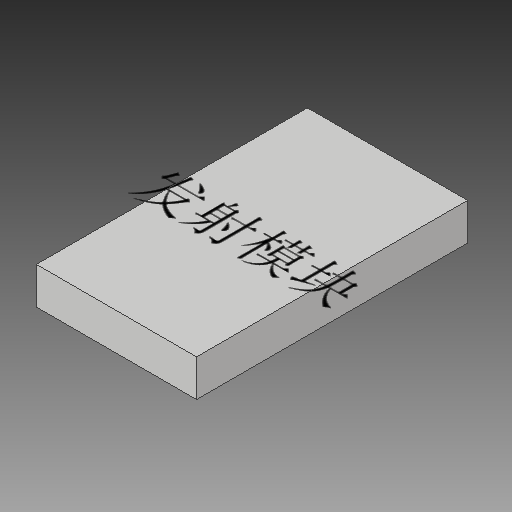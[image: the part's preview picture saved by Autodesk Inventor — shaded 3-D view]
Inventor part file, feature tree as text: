
AUTODESK INVENTOR PART (.ipt)
format: ipt  version: 2018 (Build 220112000, 112)  size: 92,160 bytes
history: native  units: mm
features: sketch x2, extrude x1
ambient origin geometry x8: Origin, YZ Plane, XZ Plane, XY Plane, X Axis, Y Axis, Z Axis, Center Point
bodies: 实体1 (feature_tree)
feature tree (3):
  extrude  "拉伸1"  Depth=13.0mm
  sketch  "草图2"  dims[d2=3.0mm d3=0.0mm]
  sketch  "草图1"  dims[d0=22.0mm d1=13.0mm]
